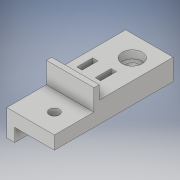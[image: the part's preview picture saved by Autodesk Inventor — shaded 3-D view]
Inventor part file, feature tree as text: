
AUTODESK INVENTOR PART (.ipt)
format: ipt  version: 2019 (Build 230136000, 136)  size: 200,192 bytes
history: native  units: in
note: dims shown in document units (in); Inventor stores cm internally (conversion verified against a paired STEP export)
features: sketch x10, extrude x8, hole x2
ambient origin geometry x8: Origin, YZ Plane, XZ Plane, XY Plane, X Axis, Y Axis, Z Axis, Center Point
bodies: Solid1 (feature_tree)
feature tree (20):
  extrude  "Extrusion1"  Depth=0.7087in
  extrude  "Extrusion3"  Depth=0.1969in TaperAngle=0.0deg
  extrude  "Extrusion4"  Depth=0.0787in
  extrude  "Extrusion6"  Depth=0.1181in TaperAngle=0.0deg
  extrude  "Extrusion7"  Depth=0.2756in
  hole  "Hole3"  [1 undecoded]
  extrude  "Extrusion10"  Depth=0.5906in
  extrude  "Extrusion11"  Depth=0.0787in
  hole  "Hole4"  [1 undecoded]
  extrude  "Extrusion12"  Depth=0.1181in TaperAngle=0.0deg
  sketch  "Sketch1"  dims[d0=1.7717in d1=0.7087in]
  sketch  "Sketch4"  dims[d2=0.315in d3=0.0in d18=0.1969in d19=0.0in]
  sketch  "Sketch5"  dims[d20=0.2362in d21=0.0787in]
  sketch  "Sketch7"  dims[d22=0.1969in d24=0.1181in d25=0.0in]
  sketch  "Sketch8"  dims[d26=0.0591in d31=0.2756in]
  sketch  "Sketch12"  dims[d34=0.3937in d35=0.0in d38=0.0394in d39=0.0in]
  sketch  "Sketch13"  dims[d57=0.0787in d58=0.5906in]
  sketch  "Sketch14"  dims[d59=0.1181in d60=0.0787in]
  sketch  "Sketch15"  dims[d61=0.0197in]
  sketch  "Sketch16"  dims[d74=0.1495in d75=0.2362in d76=0.332in d77=0.0787in d78=0.5635in d79=0.315in d80=0.8108in d81=0.1063in d82=0.0in d85=0.1181in d86=0.0in d87=0.315in d88=0.1695in d89=0.2362in d90=0.279in d91=0.0787in d92=0.5635in d93=0.315in d94=0.8108in d95=0.3in d96=0.315in d97=0.2953in d98=0.31in d100=0.1969in d101=0.0in d102=0.5906in d103=0.2953in]
note: 2 required parameter values undecoded (feature->parameter linkage not recoverable at this tier; creation-order binding heuristic only, values carry confidence <= 0.55)
